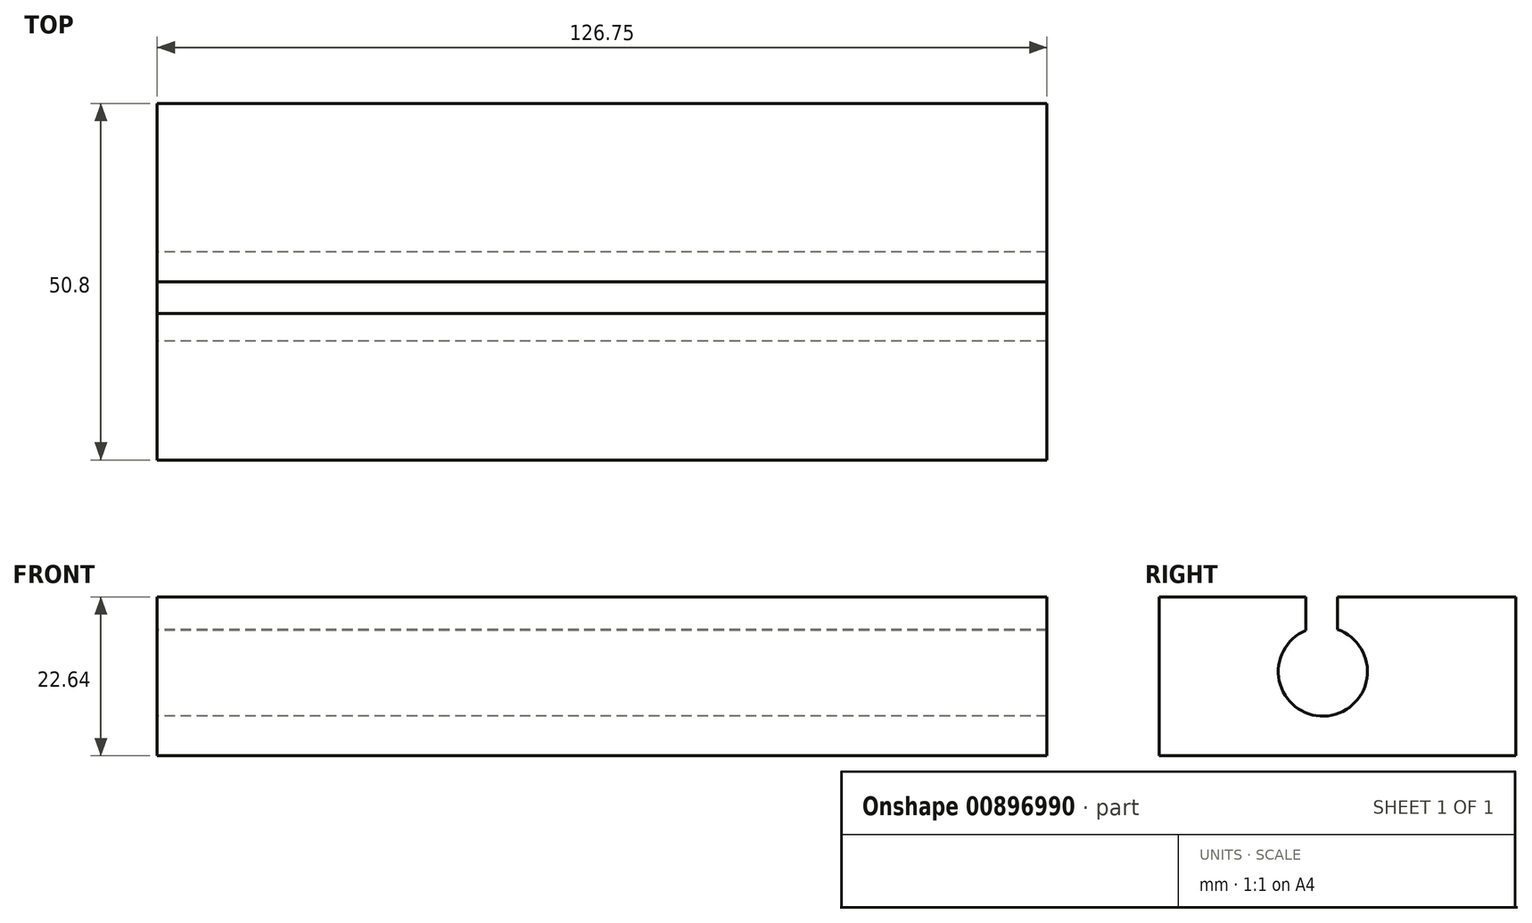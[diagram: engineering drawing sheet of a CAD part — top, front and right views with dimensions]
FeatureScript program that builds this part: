
annotation { "Feature Type Name" : "Feature", "Feature Type Description" : "" }
export const myFeature = defineFeature(function(context is Context, id is Id, definition is map)
    precondition{}
    {
        {
            var Q0;
            Q0=qCreatedBy(makeId("Front.planeOp"),FACE);
            var sketch = newSketch(context, id + "F0", { "sketchPlane" : qUnion([Q0])});
            skLineSegment(sketch, "E0.bottom", {"start": v(-55.8, 10.64) * mm, "end": v(70.96, 10.64) * mm});
            skLineSegment(sketch, "E0.top", {"start": v(-55.8, -12) * mm, "end": v(70.96, -12) * mm});
            skLineSegment(sketch, "E0.left", {"start": v(-55.8, 10.64) * mm, "end": v(-55.8, -12) * mm});
            skLineSegment(sketch, "E0.right", {"start": v(70.96, 10.64) * mm, "end": v(70.96, -12) * mm});
            skSolve(sketch);
        }
        {
            var Q0;
            Q0=makeQuery(id+"F0.imprint","IMPRINT",FACE,{"disambiguationData":[TD([[makeQuery(id+"F0.imprint","IMPRINT",EDGE,{"derivedFrom":sQuery(id+"F0.wireOp",EDGE,"E0.bottom")}),-1.0]])]});
            extrude(context, id + "F1", {"entities" : qUnion([Q0]), "depth" : 50.8 * mm, "offsetDistance" : 25.4 * mm});
        }
        {
            var Q0;
            Q0=makeQuery(id+"F1.opExtrude","SWEPT_FACE",FACE,{"disambiguationData":[OSD([sQuery(id+"F0.wireOp",EDGE,"E0.left")])]});
            var sketch = newSketch(context, id + "F2", { "sketchPlane" : qUnion([Q0])});
            skCircle(sketch, "E1", {"center": v(27.5, 0) * mm, "radius": 7.6 * mm});
            skSolve(sketch);
        }
        {
            var Q0;
            Q0=sQuery(id+"F2.wireOp",VERTEX,"E1.center");
            var Q1;
            Q1=makeQuery(id+"F1.opExtrude","SWEPT_BODY",BODY,{"disambiguationData":[OSD([sQuery(id+"F0.wireOp",EDGE,"E0.bottom"),sQuery(id+"F0.wireOp",EDGE,"E0.top"),sQuery(id+"F0.wireOp",EDGE,"E0.left"),sQuery(id+"F0.wireOp",EDGE,"E0.right")])]});
            hole(context, id + "F3", {"style" : HoleStyle.SIMPLE, "endStyle" : HoleEndStyle.THROUGH, "holeDiameter" : 12.7 * mm, "majorDiameter" : 6.35 * mm, "isTappedThrough" : true, "tappedDepth" : 12.7 * mm, "tapClearance" : 3, "locations" : qUnion([Q0]), "scope" : qUnion([Q1])});
        }
        {
            var Q0;
            Q0=makeQuery(id+"F1.opExtrude","SWEPT_FACE",FACE,{"disambiguationData":[OSD([sQuery(id+"F0.wireOp",EDGE,"E0.left")])]});
            var sketch = newSketch(context, id + "F4", { "sketchPlane" : qUnion([Q0])});
            skLineSegment(sketch, "E2.bottom", {"start": v(25.4, 10.64) * mm, "end": v(29.94, 10.64) * mm});
            skLineSegment(sketch, "E2.top", {"start": v(25.4, 5.86) * mm, "end": v(29.94, 5.86) * mm});
            skLineSegment(sketch, "E2.left", {"start": v(25.4, 10.64) * mm, "end": v(25.4, 5.86) * mm});
            skLineSegment(sketch, "E2.right", {"start": v(29.94, 10.64) * mm, "end": v(29.94, 5.86) * mm});
            skSolve(sketch);
        }
        {
            var Q0;
            {var subQ0=sQuery(id+"F4.wireOp",EDGE,"E2.bottom");Q0=makeQuery(id+"F4.imprint","IMPRINT",FACE,{"disambiguationData":[TD([[makeQuery(id+"F4.imprint","IMPRINT",EDGE,{"derivedFrom":subQ0}),1.0]])]});}
            extrude(context, id + "F5", {"entities" : qUnion([Q0]), "operationType" : NewBodyOperationType.REMOVE, "oppositeDirection" : true, "depth" : 254 * mm, "offsetDistance" : 25.4 * mm});
        }
    });
